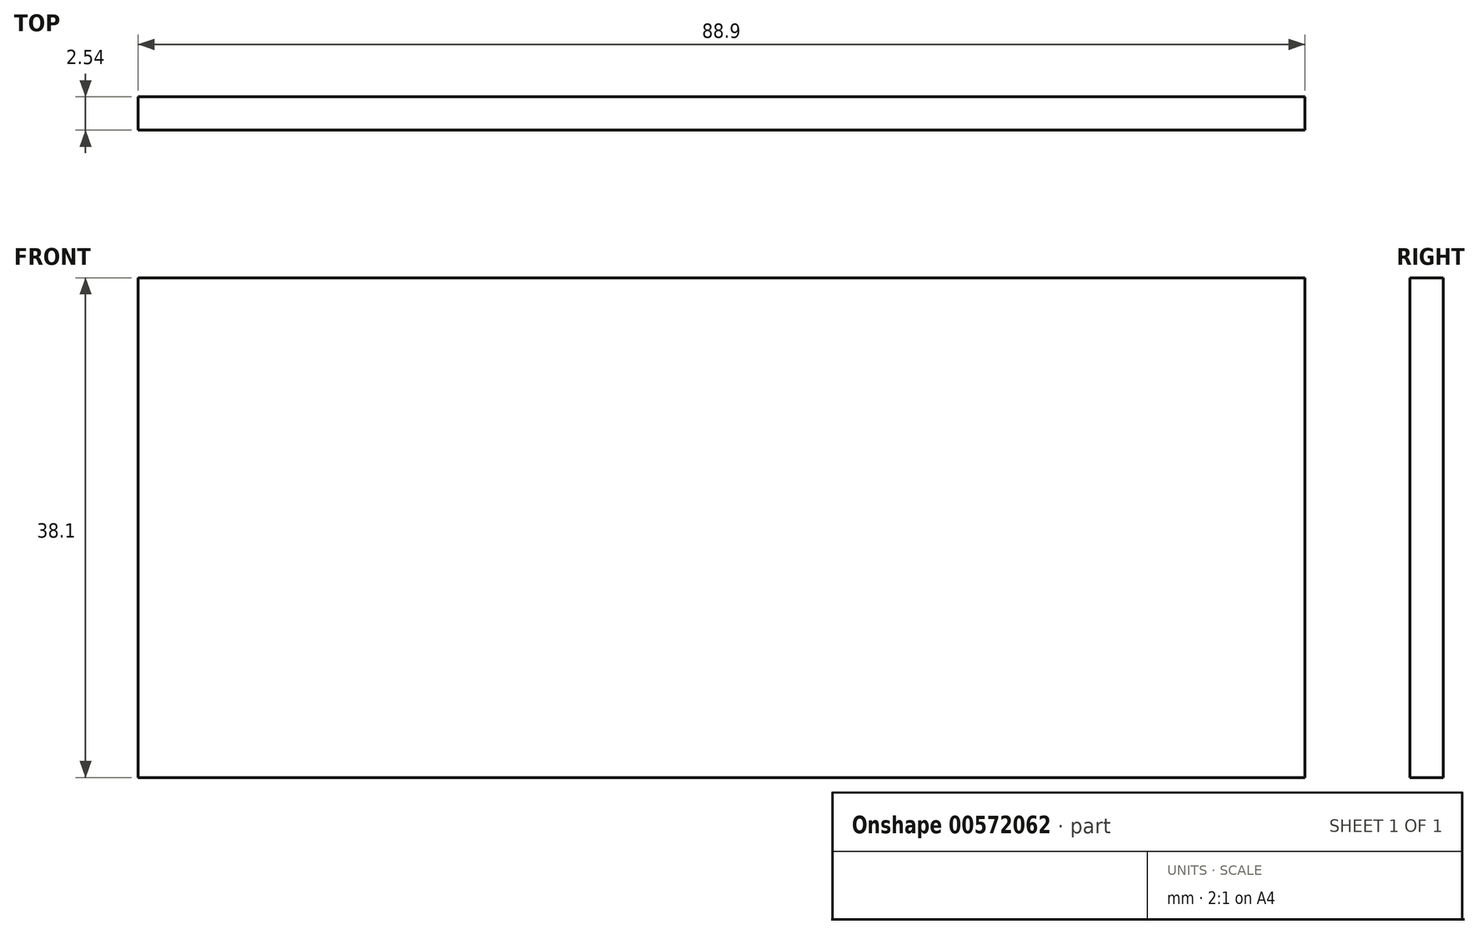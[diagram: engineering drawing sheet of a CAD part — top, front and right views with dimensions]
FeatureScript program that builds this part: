
annotation { "Feature Type Name" : "Feature", "Feature Type Description" : "" }
export const myFeature = defineFeature(function(context is Context, id is Id, definition is map)
    precondition{}
    {
        {
            var Q0;
            Q0=qCreatedBy(makeId("Front.planeOp"),FACE);
            var sketch = newSketch(context, id + "F0", { "sketchPlane" : qUnion([Q0])});
            skLineSegment(sketch, "E0.bottom", {"start": v(0, 0) * mm, "end": v(88.9, 0) * mm});
            skLineSegment(sketch, "E0.top", {"start": v(0, 38.1) * mm, "end": v(88.9, 38.1) * mm});
            skLineSegment(sketch, "E0.left", {"start": v(0, 0) * mm, "end": v(0, 38.1) * mm});
            skLineSegment(sketch, "E0.right", {"start": v(88.9, 0) * mm, "end": v(88.9, 38.1) * mm});
            skSolve(sketch);
        }
        {
            var Q0;
            Q0 = qSketchRegion(id + "F0", true);
            extrude(context, id + "F1", {"entities" : qUnion([Q0]), "depth" : 2.54 * mm, "offsetDistance" : 25.4 * mm});
        }
    });
